# Revit family: Range_Hood-BroanNutone-Pyramidal_Chimney-30in-EW4830SS
name_source: partatom
category: Specialty Equipment
units: mm (PartAtom-declared; Revit-internal decimal feet)

## family parameters
Cut with Voids When Loaded = No
Host = Face
OmniClass Number = 23.40.20.34.11.21
OmniClass Title = Fireplace and Stove Hoods
Part Type = Normal
Room Calculation Point = No
Round Connector Dimension = Use Diameter
Shared = No

## types (3) — shared parameters
Assembly Code = E1090320
Default Elevation = 4' - 0"
Depth = 1' - 7 3/4"
Description = 30in Pyramidal Chimney Range Hood
Electrical Connector = Cord Kit - Standard 120 VAC Plug
Height = 0' - 9 1/2"
Manufacturer = Broan-NuTone
Mounting Note = For best results mount 24 to 30 inches over cooking surface
Number of Poles = 1
Power Factor = 1
Product Documentation Link = https://www.broan-nutone.com
Product Name = Broan® Elite EW48 Series 30-Inch Pyramidal Chimney Range Hood, 460 Max Blower CFM
Product Page URL = https://www.broan-nutone.com
URL = https://www.broan-nutone.com
Version = 2019 – v1.0a
Voltage = 120 V
Voltage Note = 120 V
Warranty URL = https://www.broan-nutone.com
Width = 2' - 5 15/16"

## per-type parameters (varying)
| type | Finish | Model |
| 30in - Stainless Steel | Metal - Broan NuTone - Stainless Steel | EW4830SS |
| 30in - Black Stainless Steel | Metal - Broan NuTone - Stainless Steel - Black | EW4830BLS |
| 30in - White | Plastic - Broan NuTone - White | EW4830WH |

## geometry (parser evidence)
native form markers: Sweep x2
no freeform markers — native parametric forms only
